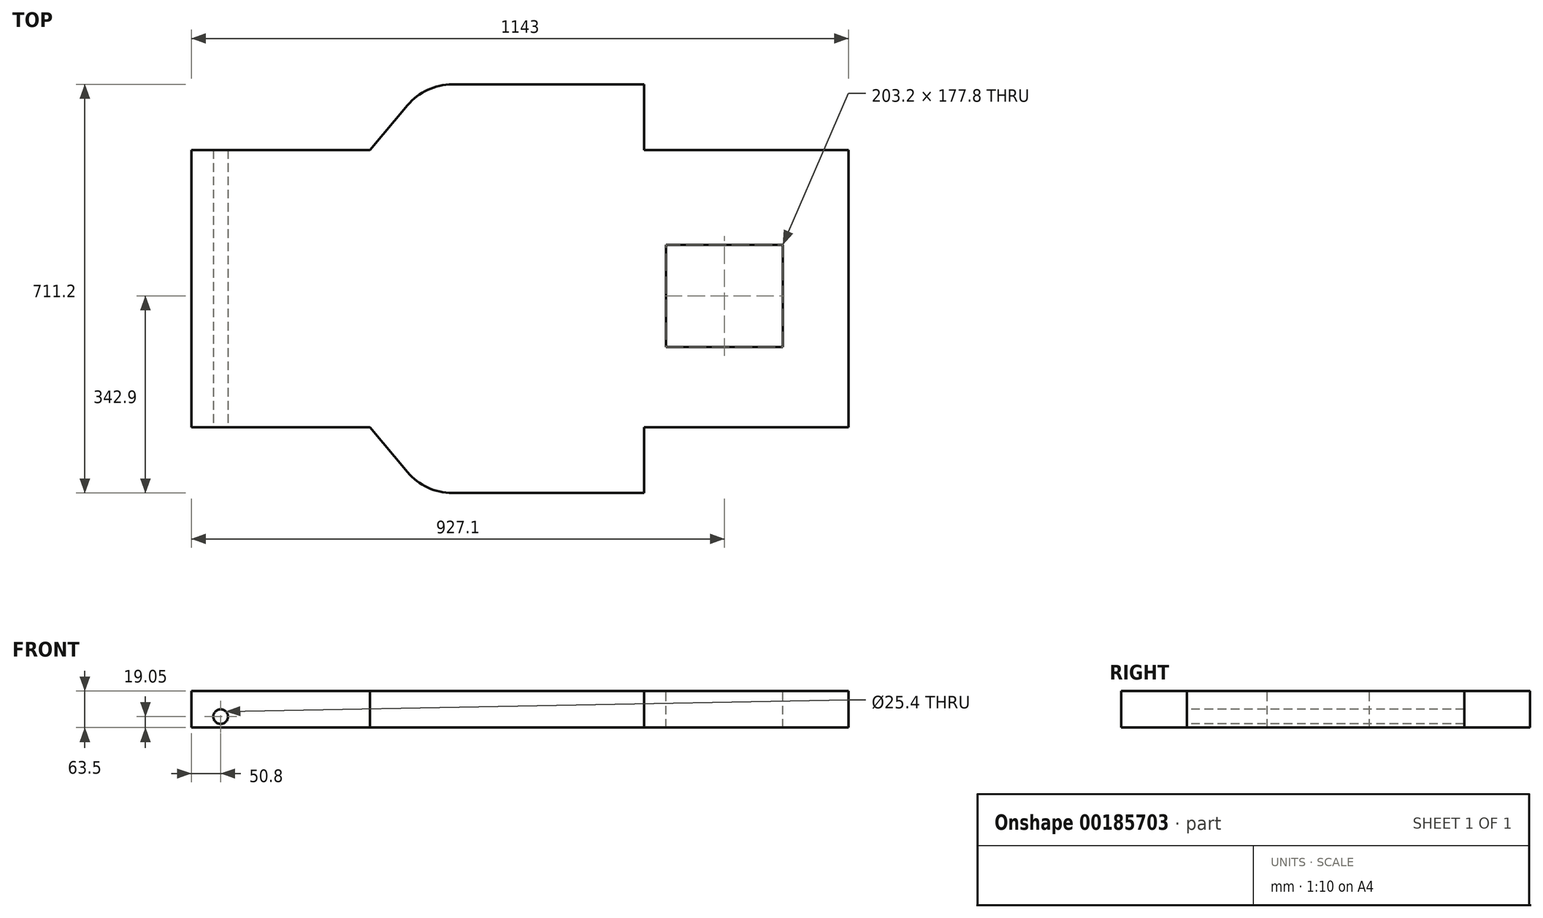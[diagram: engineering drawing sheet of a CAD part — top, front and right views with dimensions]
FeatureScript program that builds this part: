
annotation { "Feature Type Name" : "Feature", "Feature Type Description" : "" }
export const myFeature = defineFeature(function(context is Context, id is Id, definition is map)
    precondition{}
    {
        {
            var Q0;
            Q0=qCreatedBy(makeId("Top.planeOp"),FACE);
            var sketch = newSketch(context, id + "F0", { "sketchPlane" : qUnion([Q0])});
            skLineSegment(sketch, "E0.bottom", {"start": v(0, 0) * mm, "end": v(1143, 0) * mm});
            skLineSegment(sketch, "E0.top", {"start": v(0, 482.6) * mm, "end": v(1143, 482.6) * mm});
            skLineSegment(sketch, "E0.left", {"start": v(0, 0) * mm, "end": v(0, 482.6) * mm});
            skLineSegment(sketch, "E0.right", {"start": v(1143, 0) * mm, "end": v(1143, 482.6) * mm});
            skSolve(sketch);
        }
        {
            var Q0;
            Q0=makeQuery(id+"F0.imprint","IMPRINT",FACE,{"disambiguationData":[TD([[makeQuery(id+"F0.imprint","IMPRINT",EDGE,{"derivedFrom":sQuery(id+"F0.wireOp",EDGE,"E0.bottom")}),1.0]])]});
            extrude(context, id + "F1", {"entities" : qUnion([Q0]), "depth" : 63.5 * mm});
        }
        {
            var Q0;
            Q0=makeQuery(id+"F1.opExtrude","CAP_FACE",FACE,{"disambiguationData":[OSD([sQuery(id+"F0.wireOp",EDGE,"E0.bottom"),sQuery(id+"F0.wireOp",EDGE,"E0.top"),sQuery(id+"F0.wireOp",EDGE,"E0.left"),sQuery(id+"F0.wireOp",EDGE,"E0.right")])],"isStart":false});
            var sketch = newSketch(context, id + "F2", { "sketchPlane" : qUnion([Q0])});
            skLineSegment(sketch, "E1.bottom", {"start": v(825.5, 139.7) * mm, "end": v(1028.7, 139.7) * mm});
            skLineSegment(sketch, "E1.top", {"start": v(825.5, 317.5) * mm, "end": v(1028.7, 317.5) * mm});
            skLineSegment(sketch, "E1.left", {"start": v(825.5, 139.7) * mm, "end": v(825.5, 317.5) * mm});
            skLineSegment(sketch, "E1.right", {"start": v(1028.7, 139.7) * mm, "end": v(1028.7, 317.5) * mm});
            skSolve(sketch);
        }
        {
            var Q0;
            Q0 = qSketchRegion(id + "F2", true);
            extrude(context, id + "F3", {"entities" : qUnion([Q0]), "operationType" : NewBodyOperationType.REMOVE, "oppositeDirection" : true, "depth" : 63.5 * mm});
        }
        {
            var Q0;
            Q0=makeQuery(id+"F1.opExtrude","SWEPT_FACE",FACE,{"disambiguationData":[OSD([sQuery(id+"F0.wireOp",EDGE,"E0.bottom")])]});
            var sketch = newSketch(context, id + "F4", { "sketchPlane" : qUnion([Q0])});
            skCircle(sketch, "E2", {"center": v(50.8, 19.05) * mm, "radius": 12.7 * mm});
            skSolve(sketch);
        }
        {
            var Q0;
            Q0=makeQuery(id+"F4.imprint","IMPRINT",FACE,{"disambiguationData":[TD([[makeQuery(id+"F4.imprint","IMPRINT",EDGE,{"derivedFrom":sQuery(id+"F4.wireOp",EDGE,"E2")}),1.0]])]});
            extrude(context, id + "F5", {"entities" : qUnion([Q0]), "operationType" : NewBodyOperationType.REMOVE, "endBound" : BoundingType.UP_TO_NEXT, "oppositeDirection" : true, "depth" : 25.4 * mm});
        }
        {
            var Q0;
            Q0=makeQuery(id+"F1.opExtrude","CAP_FACE",FACE,{"disambiguationData":[OSD([sQuery(id+"F0.wireOp",EDGE,"E0.bottom"),sQuery(id+"F0.wireOp",EDGE,"E0.top"),sQuery(id+"F0.wireOp",EDGE,"E0.left"),sQuery(id+"F0.wireOp",EDGE,"E0.right")])],"isStart":false});
            var sketch = newSketch(context, id + "F6", { "sketchPlane" : qUnion([Q0])});
            skLineSegment(sketch, "E3", {"start": v(787.4, 482.6) * mm, "end": v(787.4, 596.9) * mm});
            skLineSegment(sketch, "E4", {"start": v(787.4, 596.9) * mm, "end": v(453.78, 596.9) * mm});
            skLineSegment(sketch, "E5", {"start": v(375.95, 560.6) * mm, "end": v(310.5, 482.6) * mm});
            skLineSegment(sketch, "E6", {"start": v(310.5, 482.6) * mm, "end": v(787.4, 482.6) * mm});
            skLineSegment(sketch, "E7", {"start": v(1143, 241.3) * mm, "end": v(0, 241.3) * mm});
            skPoint(sketch, "E8.visualSharp", {"position": v(406.4, 596.9) * mm});
            skArc(sketch, "E8.filletArc", {"start": v(453.78, 596.9) * mm, "mid": v(410.84, 587.38) * mm, "end": v(375.95, 560.6) * mm});
            skLineSegment(sketch, "E9", {"start": v(787.4, 0) * mm, "end": v(787.4, -114.3) * mm});
            skLineSegment(sketch, "E10", {"start": v(787.4, -114.3) * mm, "end": v(453.78, -114.3) * mm});
            skLineSegment(sketch, "E11", {"start": v(375.95, -78) * mm, "end": v(310.5, 0) * mm});
            skLineSegment(sketch, "E12", {"start": v(310.5, 0) * mm, "end": v(787.4, 0) * mm});
            skPoint(sketch, "E13.visualSharp", {"position": v(406.4, -114.3) * mm});
            skArc(sketch, "E13.filletArc", {"start": v(375.95, -78) * mm, "mid": v(410.84, -104.78) * mm, "end": v(453.78, -114.3) * mm});
            skSolve(sketch);
        }
        {
            var Q0;
            Q0 = qSketchRegion(id + "F6", true);
            extrude(context, id + "F7", {"entities" : qUnion([Q0]), "operationType" : NewBodyOperationType.ADD, "oppositeDirection" : true, "depth" : 63.5 * mm});
        }
    });
